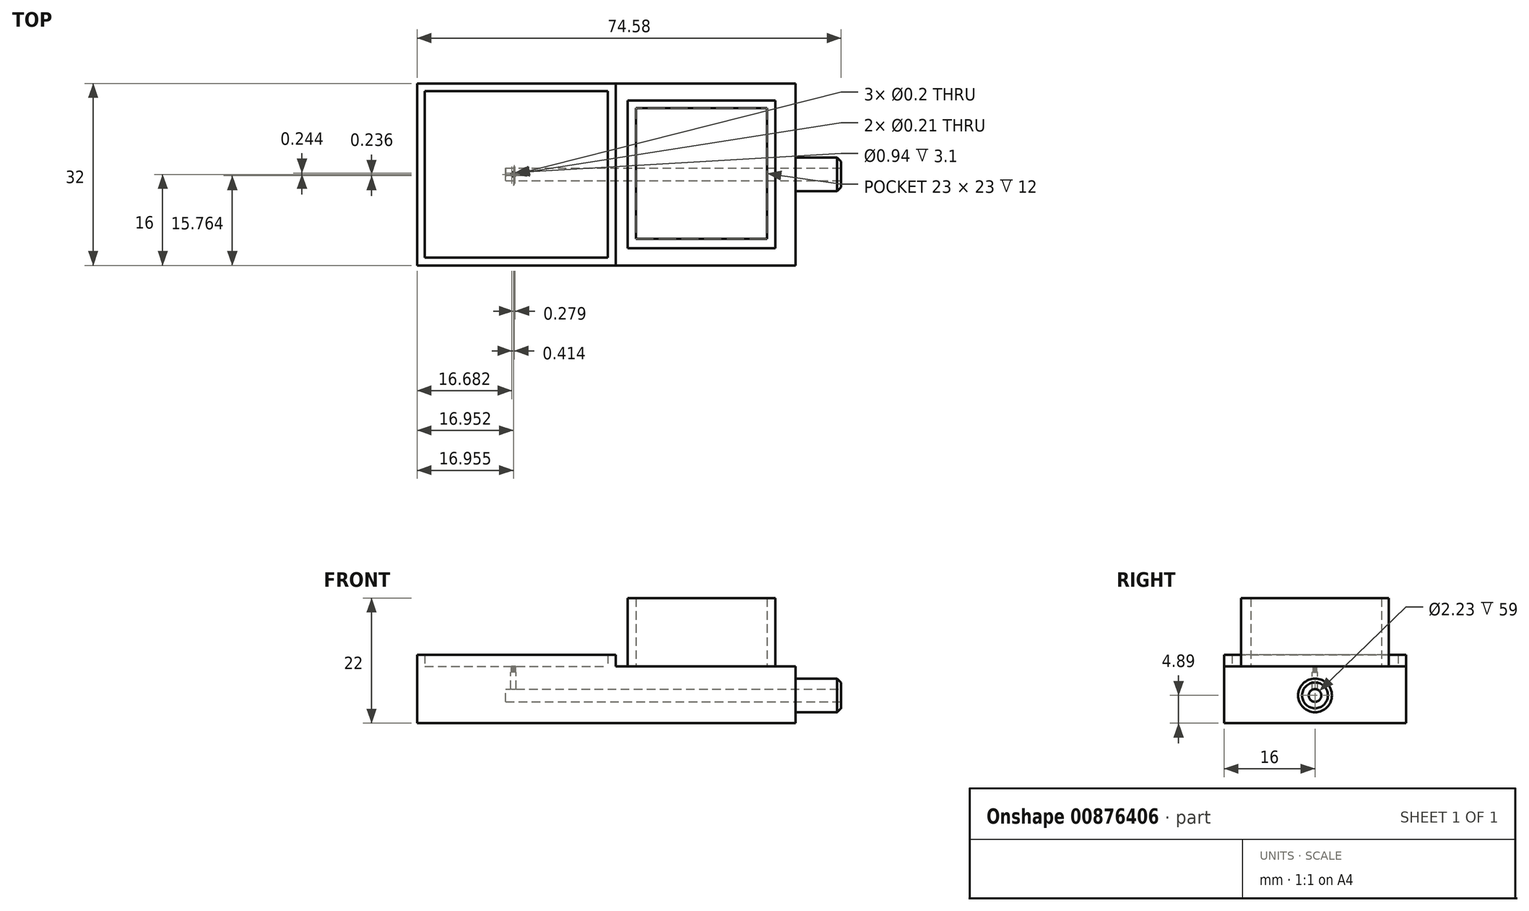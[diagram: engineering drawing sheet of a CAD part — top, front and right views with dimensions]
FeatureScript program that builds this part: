
annotation { "Feature Type Name" : "Feature", "Feature Type Description" : "" }
export const myFeature = defineFeature(function(context is Context, id is Id, definition is map)
    precondition{}
    {
        {
            var Q0;
            Q0=qCreatedBy(makeId("Top.planeOp"),FACE);
            var sketch = newSketch(context, id + "F0", { "sketchPlane" : qUnion([Q0])});
            skLineSegment(sketch, "E0.bottom", {"start": v(33.29, -16) * mm, "end": v(-33.29, -16) * mm});
            skLineSegment(sketch, "E0.top", {"start": v(33.29, 16) * mm, "end": v(-33.29, 16) * mm});
            skLineSegment(sketch, "E0.left", {"start": v(33.29, -16) * mm, "end": v(33.29, 16) * mm});
            skLineSegment(sketch, "E0.right", {"start": v(-33.29, -16) * mm, "end": v(-33.29, 16) * mm});
            skPoint(sketch, "E0.middle", {"position": v(0, 0) * mm});
            skLineSegment(sketch, "E1.bottom", {"start": v(28.24, -11.31) * mm, "end": v(5.24, -11.31) * mm});
            skLineSegment(sketch, "E1.top", {"start": v(28.24, 11.69) * mm, "end": v(5.24, 11.69) * mm});
            skLineSegment(sketch, "E1.left", {"start": v(28.24, -11.31) * mm, "end": v(28.24, 11.69) * mm});
            skLineSegment(sketch, "E1.right", {"start": v(5.24, -11.31) * mm, "end": v(5.24, 11.69) * mm});
            skLineSegment(sketch, "E2.bottom", {"start": v(29.73, -13) * mm, "end": v(3.73, -13) * mm});
            skLineSegment(sketch, "E2.top", {"start": v(29.73, 13) * mm, "end": v(3.73, 13) * mm});
            skLineSegment(sketch, "E2.left", {"start": v(29.73, -13) * mm, "end": v(29.73, 13) * mm});
            skLineSegment(sketch, "E2.right", {"start": v(3.73, -13) * mm, "end": v(3.73, 13) * mm});
            skLineSegment(sketch, "E3", {"start": v(1.64, 16) * mm, "end": v(1.64, -16) * mm});
            skLineSegment(sketch, "E4.bottom", {"start": v(-31.9, 14.64) * mm, "end": v(0.26, 14.64) * mm});
            skLineSegment(sketch, "E4.top", {"start": v(-31.9, -14.6) * mm, "end": v(0.26, -14.6) * mm});
            skLineSegment(sketch, "E4.left", {"start": v(-31.9, 14.64) * mm, "end": v(-31.9, -14.6) * mm});
            skLineSegment(sketch, "E4.right", {"start": v(0.26, 14.64) * mm, "end": v(0.26, -14.6) * mm});
            skPoint(sketch, "E5", {"position": v(-16.34, 0) * mm});
            skCircle(sketch, "E6", {"center": v(-16.34, 0) * mm, "radius": 0.1 * mm});
            skCircle(sketch, "E7", {"center": v(-16.06, 0) * mm, "radius": 0.1 * mm});
            skCircle(sketch, "E8", {"center": v(-16.6, 0) * mm, "radius": 0.1 * mm});
            skCircle(sketch, "E9", {"center": v(-16.48, -0.24) * mm, "radius": 0.1 * mm});
            skCircle(sketch, "E10", {"center": v(-16.2, -0.24) * mm, "radius": 0.1 * mm});
            skCircle(sketch, "E11", {"center": v(-16.47, 0.24) * mm, "radius": 0.1 * mm});
            skCircle(sketch, "E12", {"center": v(-16.2, 0.24) * mm, "radius": 0.1 * mm});
            skSolve(sketch);
        }
        {
            var Q0;
            Q0=makeQuery(id+"F0.imprint","IMPRINT",FACE,{"disambiguationData":[TD([[makeQuery(id+"F0.imprint","IMPRINT",EDGE,{"derivedFrom":sQuery(id+"F0.wireOp",EDGE,"E4.bottom")}),-1.0]])]});
            var Q1;
            {var subQ1=sQuery(id+"F0.wireOp",EDGE,"E0.right");Q1=makeQuery(id+"F0.imprint","IMPRINT",FACE,{"disambiguationData":[TD([[makeQuery(id+"F0.imprint","IMPRINT",EDGE,{"derivedFrom":subQ1}),-1.0]])]});}
            var Q2;
            {var subQ0=sQuery(id+"F0.wireOp",EDGE,"E0.left");Q2=makeQuery(id+"F0.imprint","IMPRINT",FACE,{"disambiguationData":[TD([[makeQuery(id+"F0.imprint","IMPRINT",EDGE,{"derivedFrom":subQ0}),1.0]])]});}
            var Q3;
            Q3=makeQuery(id+"F0.imprint","IMPRINT",FACE,{"disambiguationData":[TD([[makeQuery(id+"F0.imprint","IMPRINT",EDGE,{"derivedFrom":sQuery(id+"F0.wireOp",EDGE,"E1.bottom")}),1.0]])]});
            var Q4;
            Q4=makeQuery(id+"F0.imprint","IMPRINT",FACE,{"disambiguationData":[TD([[makeQuery(id+"F0.imprint","IMPRINT",EDGE,{"derivedFrom":sQuery(id+"F0.wireOp",EDGE,"E1.bottom")}),-1.0]])]});
            var Q5;
            Q5=makeQuery(id+"F0.imprint","IMPRINT",FACE,{"disambiguationData":[TD([[makeQuery(id+"F0.imprint","IMPRINT",EDGE,{"derivedFrom":sQuery(id+"F0.wireOp",EDGE,"E11")}),1.0]])]});
            var Q6;
            Q6=makeQuery(id+"F0.imprint","IMPRINT",FACE,{"disambiguationData":[TD([[makeQuery(id+"F0.imprint","IMPRINT",EDGE,{"derivedFrom":sQuery(id+"F0.wireOp",EDGE,"E12")}),1.0]])]});
            var Q7;
            Q7=makeQuery(id+"F0.imprint","IMPRINT",FACE,{"disambiguationData":[TD([[makeQuery(id+"F0.imprint","IMPRINT",EDGE,{"derivedFrom":sQuery(id+"F0.wireOp",EDGE,"E7")}),1.0]])]});
            var Q8;
            Q8=makeQuery(id+"F0.imprint","IMPRINT",FACE,{"disambiguationData":[TD([[makeQuery(id+"F0.imprint","IMPRINT",EDGE,{"derivedFrom":sQuery(id+"F0.wireOp",EDGE,"E10")}),1.0]])]});
            var Q9;
            Q9=makeQuery(id+"F0.imprint","IMPRINT",FACE,{"disambiguationData":[TD([[makeQuery(id+"F0.imprint","IMPRINT",EDGE,{"derivedFrom":sQuery(id+"F0.wireOp",EDGE,"E9")}),1.0]])]});
            var Q10;
            Q10=makeQuery(id+"F0.imprint","IMPRINT",FACE,{"disambiguationData":[TD([[makeQuery(id+"F0.imprint","IMPRINT",EDGE,{"derivedFrom":sQuery(id+"F0.wireOp",EDGE,"E8")}),1.0]])]});
            var Q11;
            Q11=makeQuery(id+"F0.imprint","IMPRINT",FACE,{"disambiguationData":[TD([[makeQuery(id+"F0.imprint","IMPRINT",EDGE,{"derivedFrom":sQuery(id+"F0.wireOp",EDGE,"E6")}),1.0]])]});
            extrude(context, id + "F1", {"entities" : qUnion([Q0, Q1, Q2, Q3, Q4, Q5, Q6, Q7, Q8, Q9, Q10, Q11]), "oppositeDirection" : true, "depth" : 10 * mm, "offsetDistance" : 25 * mm});
        }
        {
            var Q0;
            {var subQ1=sQuery(id+"F0.wireOp",EDGE,"E0.right");Q0=makeQuery(id+"F0.imprint","IMPRINT",FACE,{"disambiguationData":[TD([[makeQuery(id+"F0.imprint","IMPRINT",EDGE,{"derivedFrom":subQ1}),-1.0]])]});}
            extrude(context, id + "F2", {"entities" : qUnion([Q0]), "operationType" : NewBodyOperationType.ADD, "depth" : 2 * mm, "offsetDistance" : 25 * mm});
        }
        {
            var Q0;
            Q0=makeQuery(id+"F0.imprint","IMPRINT",FACE,{"disambiguationData":[TD([[makeQuery(id+"F0.imprint","IMPRINT",EDGE,{"derivedFrom":sQuery(id+"F0.wireOp",EDGE,"E1.bottom")}),1.0]])]});
            extrude(context, id + "F3", {"entities" : qUnion([Q0]), "operationType" : NewBodyOperationType.ADD, "depth" : 12 * mm, "offsetDistance" : 25 * mm});
        }
        {
            var Q0;
            Q0=makeQuery(id+"F1.opExtrude","SWEPT_FACE",FACE,{"disambiguationData":[OSD([sQuery(id+"F0.wireOp",EDGE,"E0.left")])]});
            var sketch = newSketch(context, id + "F4", { "sketchPlane" : qUnion([Q0])});
            skCircle(sketch, "E13", {"center": v(0, -5.1) * mm, "radius": 2.97 * mm});
            skCircle(sketch, "E14", {"center": v(0, -5.1) * mm, "radius": 1.12 * mm});
            skSolve(sketch);
        }
        {
            var Q0;
            Q0=makeQuery(id+"F4.imprint","IMPRINT",FACE,{"disambiguationData":[TD([[makeQuery(id+"F4.imprint","IMPRINT",EDGE,{"derivedFrom":sQuery(id+"F4.wireOp",EDGE,"E14")}),1.0]])]});
            var Q1;
            Q1=sQuery(id+"F4.wireOp",EDGE,"E14");
            extrude(context, id + "F5", {"entities" : qUnion([Q0]), "operationType" : NewBodyOperationType.REMOVE, "surfaceEntities" : qUnion([Q1]), "oppositeDirection" : true, "depth" : 51 * mm, "offsetDistance" : 25 * mm});
        }
        {
            var Q0;
            Q0=makeQuery(id+"F4.imprint","IMPRINT",FACE,{"disambiguationData":[TD([[makeQuery(id+"F4.imprint","IMPRINT",EDGE,{"derivedFrom":sQuery(id+"F4.wireOp",EDGE,"E13")}),1.0]])]});
            extrude(context, id + "F6", {"entities" : qUnion([Q0]), "operationType" : NewBodyOperationType.ADD, "depth" : 8 * mm, "offsetDistance" : 25 * mm});
        }
        {
            var Q0;
            Q0=makeQuery(id+"F6.opExtrude","CAP_EDGE",EDGE,{"disambiguationData":[OSD([sQuery(id+"F4.wireOp",EDGE,"E13")])],"isStart":false});
            chamfer(context, id + "F7", {"entities" : qUnion([Q0]), "width" : 0.7 * mm, "tangentPropagation" : true});
        }
        {
            var Q0;
            Q0=makeQuery(id+"F0.imprint","IMPRINT",FACE,{"disambiguationData":[TD([[makeQuery(id+"F0.imprint","IMPRINT",EDGE,{"derivedFrom":sQuery(id+"F0.wireOp",EDGE,"E11")}),1.0]])]});
            var Q1;
            Q1=makeQuery(id+"F0.imprint","IMPRINT",FACE,{"disambiguationData":[TD([[makeQuery(id+"F0.imprint","IMPRINT",EDGE,{"derivedFrom":sQuery(id+"F0.wireOp",EDGE,"E12")}),1.0]])]});
            var Q2;
            Q2=makeQuery(id+"F0.imprint","IMPRINT",FACE,{"disambiguationData":[TD([[makeQuery(id+"F0.imprint","IMPRINT",EDGE,{"derivedFrom":sQuery(id+"F0.wireOp",EDGE,"E7")}),1.0]])]});
            var Q3;
            Q3=makeQuery(id+"F0.imprint","IMPRINT",FACE,{"disambiguationData":[TD([[makeQuery(id+"F0.imprint","IMPRINT",EDGE,{"derivedFrom":sQuery(id+"F0.wireOp",EDGE,"E10")}),1.0]])]});
            var Q4;
            Q4=makeQuery(id+"F0.imprint","IMPRINT",FACE,{"disambiguationData":[TD([[makeQuery(id+"F0.imprint","IMPRINT",EDGE,{"derivedFrom":sQuery(id+"F0.wireOp",EDGE,"E9")}),1.0]])]});
            var Q5;
            Q5=makeQuery(id+"F0.imprint","IMPRINT",FACE,{"disambiguationData":[TD([[makeQuery(id+"F0.imprint","IMPRINT",EDGE,{"derivedFrom":sQuery(id+"F0.wireOp",EDGE,"E8")}),1.0]])]});
            var Q6;
            Q6=makeQuery(id+"F0.imprint","IMPRINT",FACE,{"disambiguationData":[TD([[makeQuery(id+"F0.imprint","IMPRINT",EDGE,{"derivedFrom":sQuery(id+"F0.wireOp",EDGE,"E6")}),1.0]])]});
            extrude(context, id + "F8", {"entities" : qUnion([Q0, Q1, Q2, Q3, Q4, Q5, Q6]), "operationType" : NewBodyOperationType.REMOVE, "oppositeDirection" : true, "depth" : 1 * mm, "offsetDistance" : 25 * mm});
        }
        {
            var Q0;
            {var subQ0=sQuery(id+"F0.wireOp",EDGE,"E0.left");Q0=makeQuery(id+"F0.imprint","IMPRINT",FACE,{"disambiguationData":[TD([[makeQuery(id+"F0.imprint","IMPRINT",EDGE,{"derivedFrom":subQ0}),1.0]])]});}
            cPlane(context, id + "F9", {"entities" : qUnion([Q0]), "cplaneType" : CPlaneType.OFFSET, "offset" : 1 * mm, "oppositeDirection" : true, "width" : 150 * mm, "height" : 150 * mm});
        }
        {
            var Q0;
            Q0=qCreatedBy(id+"F9.planeOp",FACE);
            var sketch = newSketch(context, id + "F10", { "sketchPlane" : qUnion([Q0])});
            skCircle(sketch, "E15", {"center": v(-16.33, 0) * mm, "radius": 0.47 * mm});
            skSolve(sketch);
        }
        {
            var Q0;
            Q0=makeQuery(id+"F10.imprint","IMPRINT",FACE,{"disambiguationData":[TD([[makeQuery(id+"F10.imprint","IMPRINT",EDGE,{"derivedFrom":sQuery(id+"F10.wireOp",EDGE,"E15")}),1.0]])]});
            extrude(context, id + "F11", {"entities" : qUnion([Q0]), "operationType" : NewBodyOperationType.REMOVE, "oppositeDirection" : true, "depth" : 4 * mm, "offsetDistance" : 25 * mm});
        }
    });
